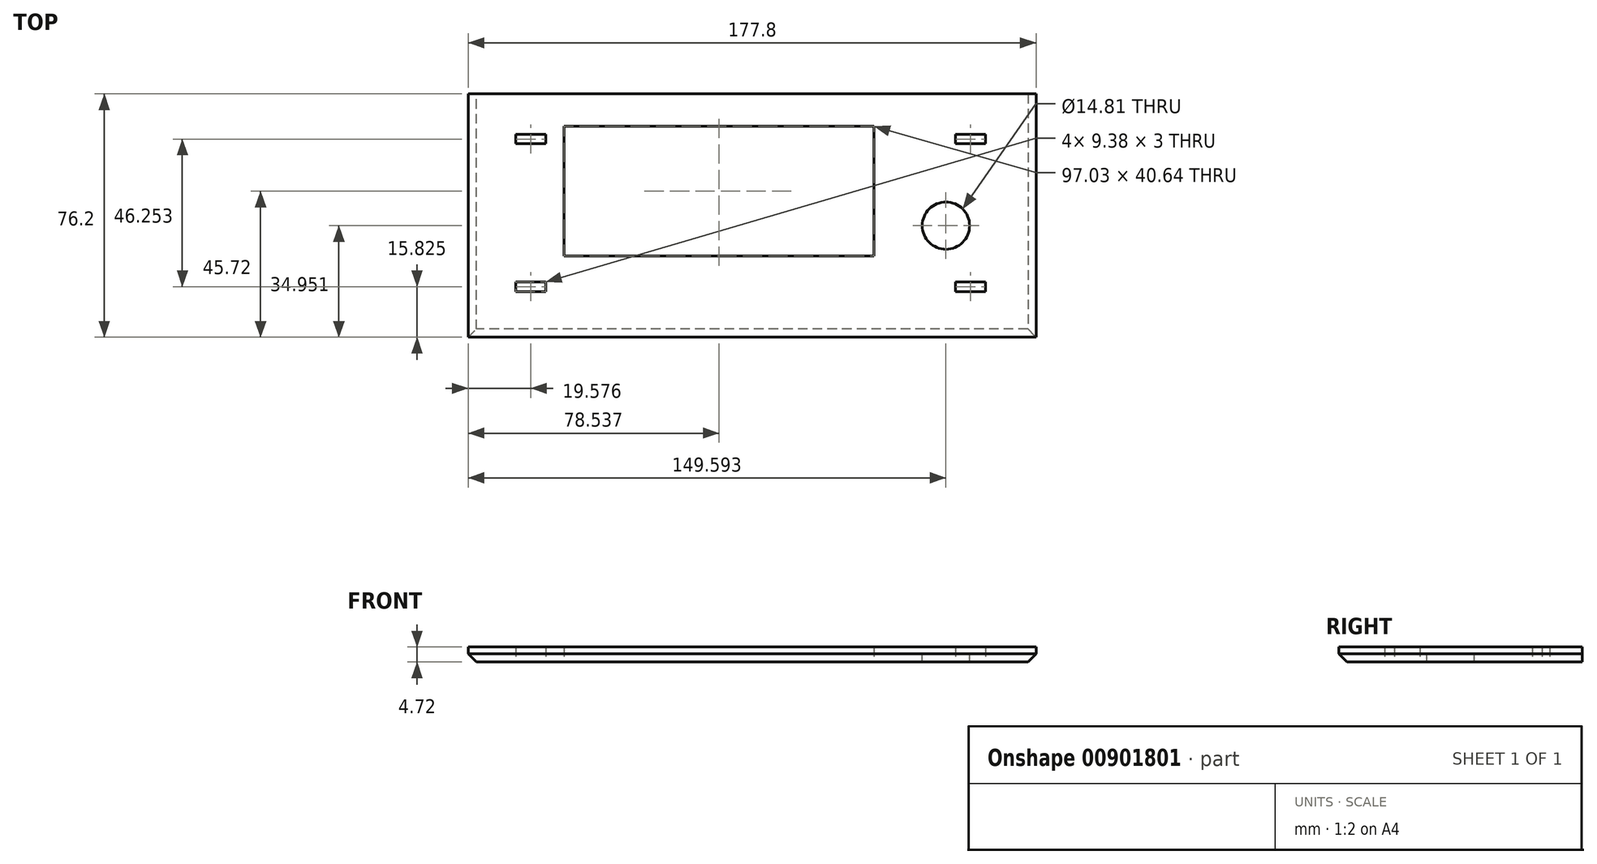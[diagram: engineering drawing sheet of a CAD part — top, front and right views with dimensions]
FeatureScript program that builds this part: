
annotation { "Feature Type Name" : "Feature", "Feature Type Description" : "" }
export const myFeature = defineFeature(function(context is Context, id is Id, definition is map)
    precondition{}
    {
        {
            var Q0;
            Q0=qCreatedBy(makeId("Top.planeOp"),FACE);
            var sketch = newSketch(context, id + "F0", { "sketchPlane" : qUnion([Q0])});
            skLineSegment(sketch, "E0.bottom", {"start": v(0, -2.67) * mm, "end": v(177.8, -2.67) * mm});
            skLineSegment(sketch, "E0.top", {"start": v(0, 73.53) * mm, "end": v(177.8, 73.53) * mm});
            skLineSegment(sketch, "E0.left", {"start": v(0, -2.67) * mm, "end": v(0, 73.53) * mm});
            skLineSegment(sketch, "E0.right", {"start": v(177.8, -2.67) * mm, "end": v(177.8, 73.53) * mm});
            skLineSegment(sketch, "E1.bottom", {"start": v(30.02, 63.37) * mm, "end": v(127.05, 63.37) * mm});
            skLineSegment(sketch, "E1.top", {"start": v(30.02, 22.73) * mm, "end": v(127.05, 22.73) * mm});
            skLineSegment(sketch, "E1.left", {"start": v(30.02, 63.37) * mm, "end": v(30.02, 22.73) * mm});
            skLineSegment(sketch, "E1.right", {"start": v(127.05, 63.37) * mm, "end": v(127.05, 22.73) * mm});
            skSolve(sketch);
        }
        {
            var Q0;
            Q0=makeQuery(id+"F0.imprint","IMPRINT",FACE,{"disambiguationData":[TD([[makeQuery(id+"F0.imprint","IMPRINT",EDGE,{"derivedFrom":sQuery(id+"F0.wireOp",EDGE,"E0.bottom")}),1.0]])]});
            extrude(context, id + "F1", {"entities" : qUnion([Q0]), "depth" : 4.72 * mm, "offsetDistance" : 25.4 * mm});
        }
        {
            var Q0;
            Q0=makeQuery(id+"F1.opExtrude","CAP_FACE",FACE,{"disambiguationData":[OSD([sQuery(id+"F0.wireOp",EDGE,"E0.bottom"),sQuery(id+"F0.wireOp",EDGE,"E0.top"),sQuery(id+"F0.wireOp",EDGE,"E0.left"),sQuery(id+"F0.wireOp",EDGE,"E0.right"),sQuery(id+"F0.wireOp",EDGE,"E1.bottom"),sQuery(id+"F0.wireOp",EDGE,"E1.top"),sQuery(id+"F0.wireOp",EDGE,"E1.left"),sQuery(id+"F0.wireOp",EDGE,"E1.right")])],"isStart":false});
            var sketch = newSketch(context, id + "F2", { "sketchPlane" : qUnion([Q0])});
            skCircle(sketch, "E2", {"center": v(149.6, 32.28) * mm, "radius": 7.4 * mm});
            skSolve(sketch);
        }
        {
            var Q0;
            Q0=makeQuery(id+"F2.imprint","IMPRINT",FACE,{"disambiguationData":[TD([[makeQuery(id+"F2.imprint","IMPRINT",EDGE,{"derivedFrom":sQuery(id+"F2.wireOp",EDGE,"E2")}),1.0]])]});
            extrude(context, id + "F3", {"entities" : qUnion([Q0]), "operationType" : NewBodyOperationType.REMOVE, "oppositeDirection" : true, "depth" : 25.4 * mm, "offsetDistance" : 25.4 * mm});
        }
        {
            var Q0;
            Q0=makeQuery(id+"F1.opExtrude","CAP_EDGE",EDGE,{"disambiguationData":[OSD([sQuery(id+"F0.wireOp",EDGE,"E0.left")])],"isStart":true});
            var Q1;
            Q1=makeQuery(id+"F1.opExtrude","CAP_EDGE",EDGE,{"disambiguationData":[OSD([sQuery(id+"F0.wireOp",EDGE,"E0.bottom")])],"isStart":true});
            var Q2;
            Q2=makeQuery(id+"F1.opExtrude","CAP_EDGE",EDGE,{"disambiguationData":[OSD([sQuery(id+"F0.wireOp",EDGE,"E0.right")])],"isStart":true});
            chamfer(context, id + "F4", {"entities" : qUnion([Q0, Q1, Q2]), "width" : 2.54 * mm, "tangentPropagation" : true});
        }
        {
            var Q0;
            Q0=makeQuery(id+"F1.opExtrude","CAP_FACE",FACE,{"disambiguationData":[OSD([sQuery(id+"F0.wireOp",EDGE,"E0.bottom"),sQuery(id+"F0.wireOp",EDGE,"E0.top"),sQuery(id+"F0.wireOp",EDGE,"E0.left"),sQuery(id+"F0.wireOp",EDGE,"E0.right"),sQuery(id+"F0.wireOp",EDGE,"E1.bottom"),sQuery(id+"F0.wireOp",EDGE,"E1.top"),sQuery(id+"F0.wireOp",EDGE,"E1.left"),sQuery(id+"F0.wireOp",EDGE,"E1.right")])],"isStart":true});
            var sketch = newSketch(context, id + "F5", { "sketchPlane" : qUnion([Q0])});
            skLineSegment(sketch, "E3.bottom", {"start": v(14.88, -11.66) * mm, "end": v(24.27, -11.66) * mm});
            skLineSegment(sketch, "E3.top", {"start": v(14.88, -14.65) * mm, "end": v(24.27, -14.65) * mm});
            skLineSegment(sketch, "E3.left", {"start": v(14.88, -11.66) * mm, "end": v(14.88, -14.65) * mm});
            skLineSegment(sketch, "E3.right", {"start": v(24.27, -11.66) * mm, "end": v(24.27, -14.65) * mm});
            skLineSegment(sketch, "E4.0.1.0", {"start": v(14.88, -57.9) * mm, "end": v(24.27, -57.9) * mm});
            skLineSegment(sketch, "E4.0.1.1", {"start": v(14.88, -60.9) * mm, "end": v(24.27, -60.9) * mm});
            skLineSegment(sketch, "E4.0.1.2", {"start": v(14.88, -57.9) * mm, "end": v(14.88, -60.9) * mm});
            skLineSegment(sketch, "E4.0.1.3", {"start": v(24.27, -57.9) * mm, "end": v(24.27, -60.9) * mm});
            skLineSegment(sketch, "E4.1.0.0", {"start": v(152.58, -11.66) * mm, "end": v(161.96, -11.66) * mm});
            skLineSegment(sketch, "E4.1.0.1", {"start": v(152.58, -14.65) * mm, "end": v(161.96, -14.65) * mm});
            skLineSegment(sketch, "E4.1.0.2", {"start": v(152.58, -11.66) * mm, "end": v(152.58, -14.65) * mm});
            skLineSegment(sketch, "E4.1.0.3", {"start": v(161.96, -11.66) * mm, "end": v(161.96, -14.65) * mm});
            skLineSegment(sketch, "E4.1.1.0", {"start": v(152.58, -57.9) * mm, "end": v(161.96, -57.9) * mm});
            skLineSegment(sketch, "E4.1.1.1", {"start": v(152.58, -60.9) * mm, "end": v(161.96, -60.9) * mm});
            skLineSegment(sketch, "E4.1.1.2", {"start": v(152.58, -57.9) * mm, "end": v(152.58, -60.9) * mm});
            skLineSegment(sketch, "E4.1.1.3", {"start": v(161.96, -57.9) * mm, "end": v(161.96, -60.9) * mm});
            skLineSegment(sketch, "E4.direction1", {"start": v(14.88, -11.66) * mm, "end": v(152.58, -11.66) * mm, "construction": true});
            skLineSegment(sketch, "E4.direction2", {"start": v(14.88, -11.66) * mm, "end": v(14.88, -57.9) * mm, "construction": true});
            skSolve(sketch);
        }
        {
            var Q0;
            Q0 = qSketchRegion(id + "F5", true);
            extrude(context, id + "F6", {"entities" : qUnion([Q0]), "operationType" : NewBodyOperationType.REMOVE, "oppositeDirection" : true, "depth" : 25.4 * mm, "offsetDistance" : 25.4 * mm});
        }
    });
